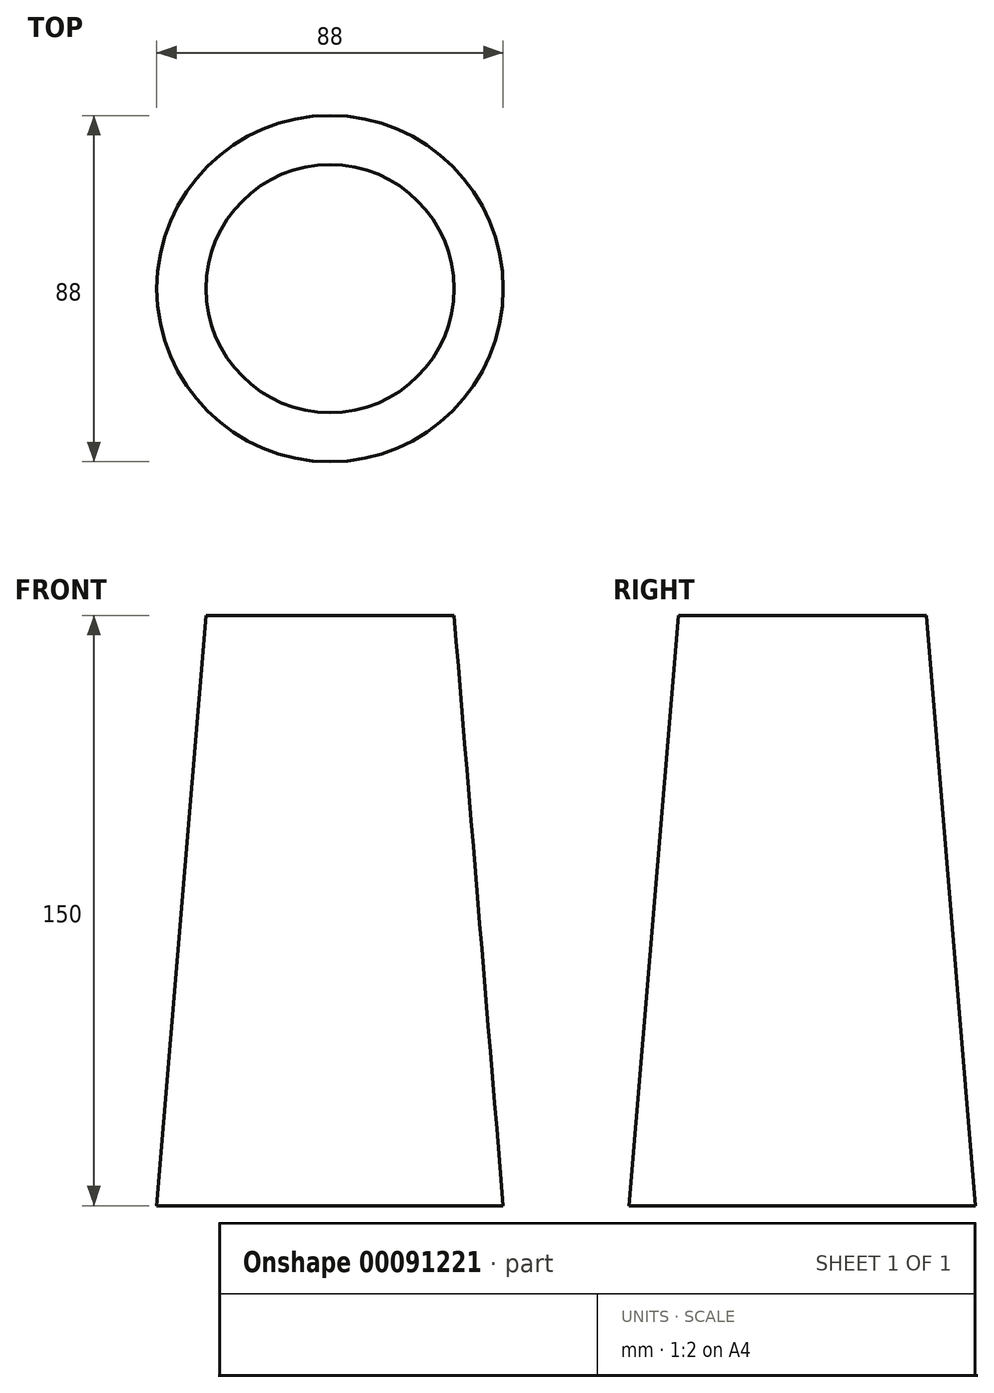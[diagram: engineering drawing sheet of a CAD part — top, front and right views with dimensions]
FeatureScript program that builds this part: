
annotation { "Feature Type Name" : "Feature", "Feature Type Description" : "" }
export const myFeature = defineFeature(function(context is Context, id is Id, definition is map)
    precondition{}
    {
        {
            var Q0;
            Q0=qCreatedBy(makeId("Top.planeOp"),FACE);
            var sketch = newSketch(context, id + "F0", { "sketchPlane" : qUnion([Q0])});
            skCircle(sketch, "E0", {"center": v(0, 0) * mm, "radius": 31.5 * mm});
            skSolve(sketch);
        }
        {
            var Q0;
            Q0=qCreatedBy(makeId("Top.planeOp"),FACE);
            cPlane(context, id + "F1", {"entities" : qUnion([Q0]), "cplaneType" : CPlaneType.OFFSET, "offset" : 150 * mm, "oppositeDirection" : true, "width" : 150 * mm, "height" : 150 * mm});
        }
        {
            var Q0;
            Q0=qCreatedBy(id+"F1.planeOp",FACE);
            var sketch = newSketch(context, id + "F2", { "sketchPlane" : qUnion([Q0])});
            skCircle(sketch, "E1", {"center": v(0, 0) * mm, "radius": 44 * mm});
            skSolve(sketch);
        }
        {
            var Q0;
            Q0=makeQuery(id+"F0.imprint","IMPRINT",FACE,{"disambiguationData":[TD([[makeQuery(id+"F0.imprint","IMPRINT",EDGE,{"derivedFrom":sQuery(id+"F0.wireOp",EDGE,"E0")}),1.0]])]});
            var Q1;
            Q1=makeQuery(id+"F2.imprint","IMPRINT",FACE,{"disambiguationData":[TD([[makeQuery(id+"F2.imprint","IMPRINT",EDGE,{"derivedFrom":sQuery(id+"F2.wireOp",EDGE,"E1")}),1.0]])]});
            loft(context, id + "F3", {"sheetProfilesArray" : [{ "sheetProfileEntities" : qUnion([Q0]) }, { "sheetProfileEntities" : qUnion([Q1]) }]});
        }
    });
